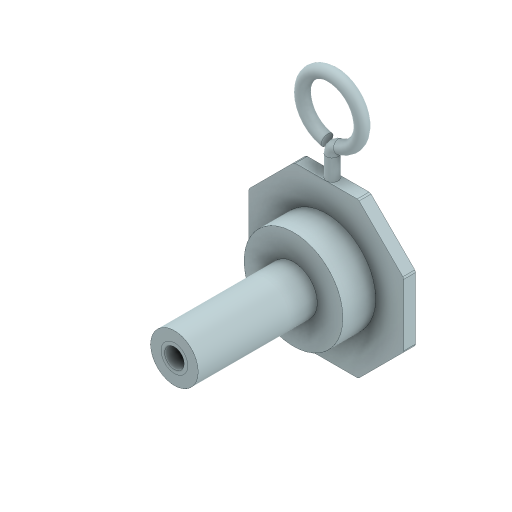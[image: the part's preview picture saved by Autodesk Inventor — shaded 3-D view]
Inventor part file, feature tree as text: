
AUTODESK INVENTOR PART (.ipt)
format: ipt  version: 2023 (Build 270158000, 158)  size: 714,752 bytes
history: native  units: mm
features: other x1, thread x1
ambient origin geometry x8: Origin, YZ Plane, XZ Plane, XY Plane, X Axis, Y Axis, Z Axis, Center Point
bodies: Solid1 (feature_tree), Solid2 (feature_tree)
feature tree (2):
  other  "MSL_Top.stp_1_"
  thread  "Gewinde1"  [1 undecoded]
note: 1 required parameter value undecoded (feature->parameter linkage not recoverable at this tier; creation-order binding heuristic only, values carry confidence <= 0.55)
